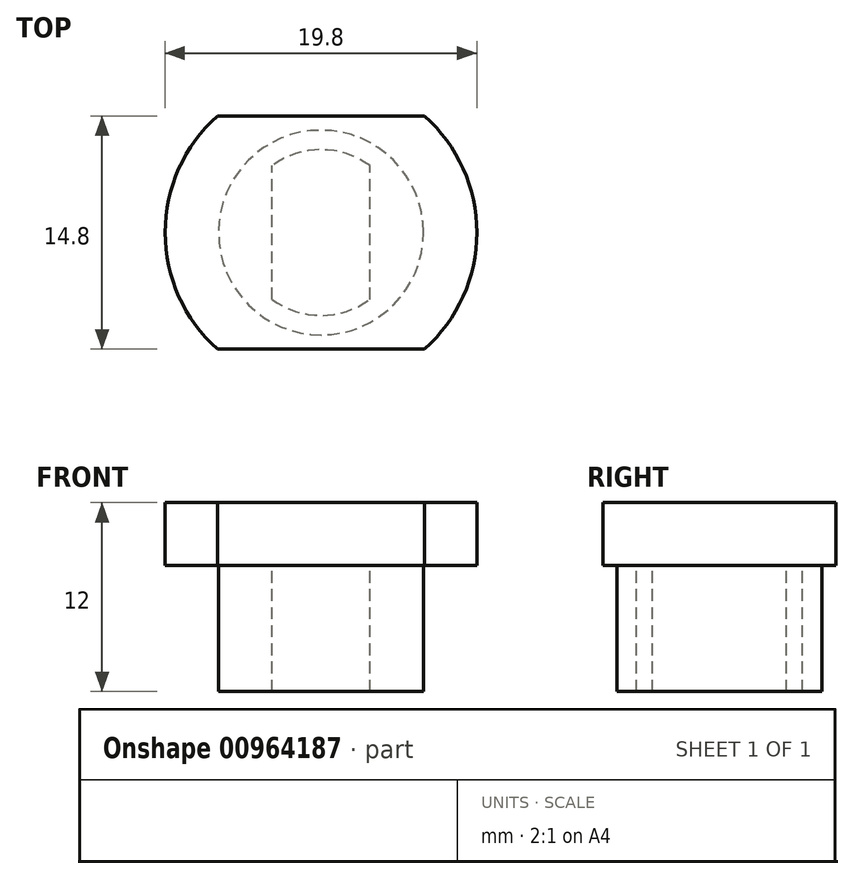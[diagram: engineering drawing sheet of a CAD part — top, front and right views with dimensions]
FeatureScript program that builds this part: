
annotation { "Feature Type Name" : "Feature", "Feature Type Description" : "" }
export const myFeature = defineFeature(function(context is Context, id is Id, definition is map)
    precondition{}
    {
        {
            var Q0;
            Q0=qCreatedBy(makeId("Top.planeOp"),FACE);
            var sketch = newSketch(context, id + "F0", { "sketchPlane" : qUnion([Q0])});
            skCircle(sketch, "E0", {"center": v(0, 0) * mm, "radius": 6.5 * mm});
            skSolve(sketch);
        }
        {
            var Q0;
            Q0 = qSketchRegion(id + "F0", true);
            extrude(context, id + "F1", {"entities" : qUnion([Q0]), "depth" : 8 * mm, "offsetDistance" : 25 * mm});
        }
        {
            var Q0;
            Q0=makeQuery(id+"F1.opExtrude","CAP_FACE",FACE,{"disambiguationData":[OSD([sQuery(id+"F0.wireOp",EDGE,"E0")])],"isStart":false});
            var sketch = newSketch(context, id + "F2", { "sketchPlane" : qUnion([Q0])});
            skLineSegment(sketch, "E1.left", {"start": v(-3.1, 4.25) * mm, "end": v(-3.1, -4.25) * mm});
            skLineSegment(sketch, "E1.right", {"start": v(3.1, 4.25) * mm, "end": v(3.1, -4.25) * mm});
            skArc(sketch, "E2", {"start": v(3.1, 4.25) * mm, "mid": v(0, 5.26) * mm, "end": v(-3.1, 4.25) * mm});
            skArc(sketch, "E3", {"start": v(-3.1, -4.25) * mm, "mid": v(0, -5.26) * mm, "end": v(3.1, -4.25) * mm});
            skLineSegment(sketch, "E4", {"start": v(-3.1, 4.25) * mm, "end": v(3.1, 4.25) * mm, "construction": true});
            skLineSegment(sketch, "E5", {"start": v(-3.1, -4.25) * mm, "end": v(3.1, -4.25) * mm, "construction": true});
            skSolve(sketch);
        }
        {
            var Q0;
            Q0 = qSketchRegion(id + "F2", true);
            extrude(context, id + "F3", {"entities" : qUnion([Q0]), "operationType" : NewBodyOperationType.REMOVE, "endBound" : BoundingType.UP_TO_NEXT, "oppositeDirection" : true, "depth" : 25 * mm, "offsetDistance" : 25 * mm});
        }
        {
            var Q0;
            Q0=makeQuery(id+"F1.opExtrude","CAP_FACE",FACE,{"disambiguationData":[OSD([sQuery(id+"F0.wireOp",EDGE,"E0")])],"isStart":false});
            var sketch = newSketch(context, id + "F4", { "sketchPlane" : qUnion([Q0])});
            skCircle(sketch, "E6", {"center": v(0, 0) * mm, "radius": 9.9 * mm});
            skSolve(sketch);
        }
        {
            var Q0;
            Q0 = qSketchRegion(id + "F4", true);
            extrude(context, id + "F5", {"entities" : qUnion([Q0]), "operationType" : NewBodyOperationType.ADD, "depth" : 4 * mm, "offsetDistance" : 25 * mm});
        }
        {
            var Q0;
            Q0=makeQuery(id+"F5.opExtrude","CAP_FACE",FACE,{"disambiguationData":[OSD([sQuery(id+"F4.wireOp",EDGE,"E6")])],"isStart":false});
            var sketch = newSketch(context, id + "F6", { "sketchPlane" : qUnion([Q0])});
            skLineSegment(sketch, "E7", {"start": v(-6.58, 7.4) * mm, "end": v(6.58, 7.4) * mm});
            skArc(sketch, "E8", {"start": v(6.58, 7.4) * mm, "mid": v(0, 9.9) * mm, "end": v(-6.58, 7.4) * mm});
            skLineSegment(sketch, "E9.MirrorCS", {"start": v(-6.58, -7.4) * mm, "end": v(6.58, -7.4) * mm});
            skArc(sketch, "E10.MirrorCS", {"start": v(6.58, -7.4) * mm, "mid": v(0, -9.9) * mm, "end": v(-6.58, -7.4) * mm});
            skSolve(sketch);
        }
        {
            var Q0;
            Q0 = qSketchRegion(id + "F6", true);
            extrude(context, id + "F7", {"entities" : qUnion([Q0]), "operationType" : NewBodyOperationType.REMOVE, "endBound" : BoundingType.UP_TO_NEXT, "oppositeDirection" : true, "depth" : 25 * mm, "offsetDistance" : 25 * mm});
        }
    });
